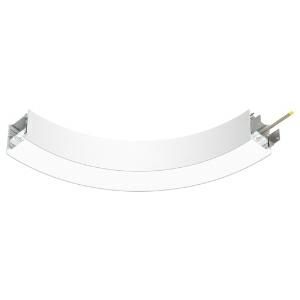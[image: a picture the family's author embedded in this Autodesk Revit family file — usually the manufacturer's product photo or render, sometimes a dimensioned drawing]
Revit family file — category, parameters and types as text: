
# Revit family: super-g_slim_super_g_slim_800_90deg_hl_ps_led__12w_1580lm_3000k_cri_80_430-1640_560c
name_source: partatom
category: Leuchten
revit_build: Autodesk Revit 2016 (Build: 20190508_0715(x64)
units: mm (PartAtom-declared; Revit-internal decimal feet)

## family parameters
Basisbauteil = Fläche
Beim Laden mit Abzugskörper schneiden = Nein
Bemaßung runder Anschluss = Durchmesser verwenden
Gemeinsam genutzt = Nein
Lichtquelle = Nein
Raumberechnungspunkt = Nein
Teiletyp = Normal

## types (1)
- 430-1640-D01 (1 x LED, 480 lm, 3000K)
    Approval mark = CE
    Beschreibung = The insert consists of aluminum-extruded profile. Charming SOFT-EDGE design ensure unparalleled styling. The ballast is integrated and allows for an operation with 220-240V (50/60Hz). SUPER-G SLIM (# 430-1640) ist not dimmable (on/off).
    CIE Flux Codes = 48 79 96 100 71
    Color Rendering = 1B/80…89
    Color Temperature = 3000K
    Height = 90 mm
    Hersteller = Prolicht
    Lamp Light Flux = 480 lm
    Lamp count = 1
    Lampe = 1 x LED
    Length = 144 mm
    Luminous efficacy = 103 lm/W
    ModVariant = Nein
    Modell = 430-1640
    Mounting Place = Ceiling
    Mounting Type = Pendant
    Number of Poles = 1
    OnlyDefault = Ja
    Power Factor = 1
    Product Name = SUPER-G SLIM__SUPER G SLIM 800/90° HL PS LED: 12W 1580lm 3000K CRI:80
    Product group = Suspended profile systems
    ProductGroupID = 944
    Protection Class = Protection class I
    Protection Degree = IP 20
    RLX_Detail_Level = 1
    RlxData = <blob elided: 39977 chars, md5=d6c120dc>
    Scheinlast = 13 VA
    Socket = socket
    Standby Power = 0 W
    System Light Flux = 1361 lm
    System Power = 13 W
    Typenbild = 430-1640.jpg
    URL = http://relux.com
    VarID = 430-1640-d01
    Voltage = 0 V
    Vorgabe-Ansicht = 1800 mm
    Weight = 0.00 kg
    Width = 65 mm

## geometry (parser evidence)
native form markers: Sweep x22
no freeform markers — native parametric forms only
